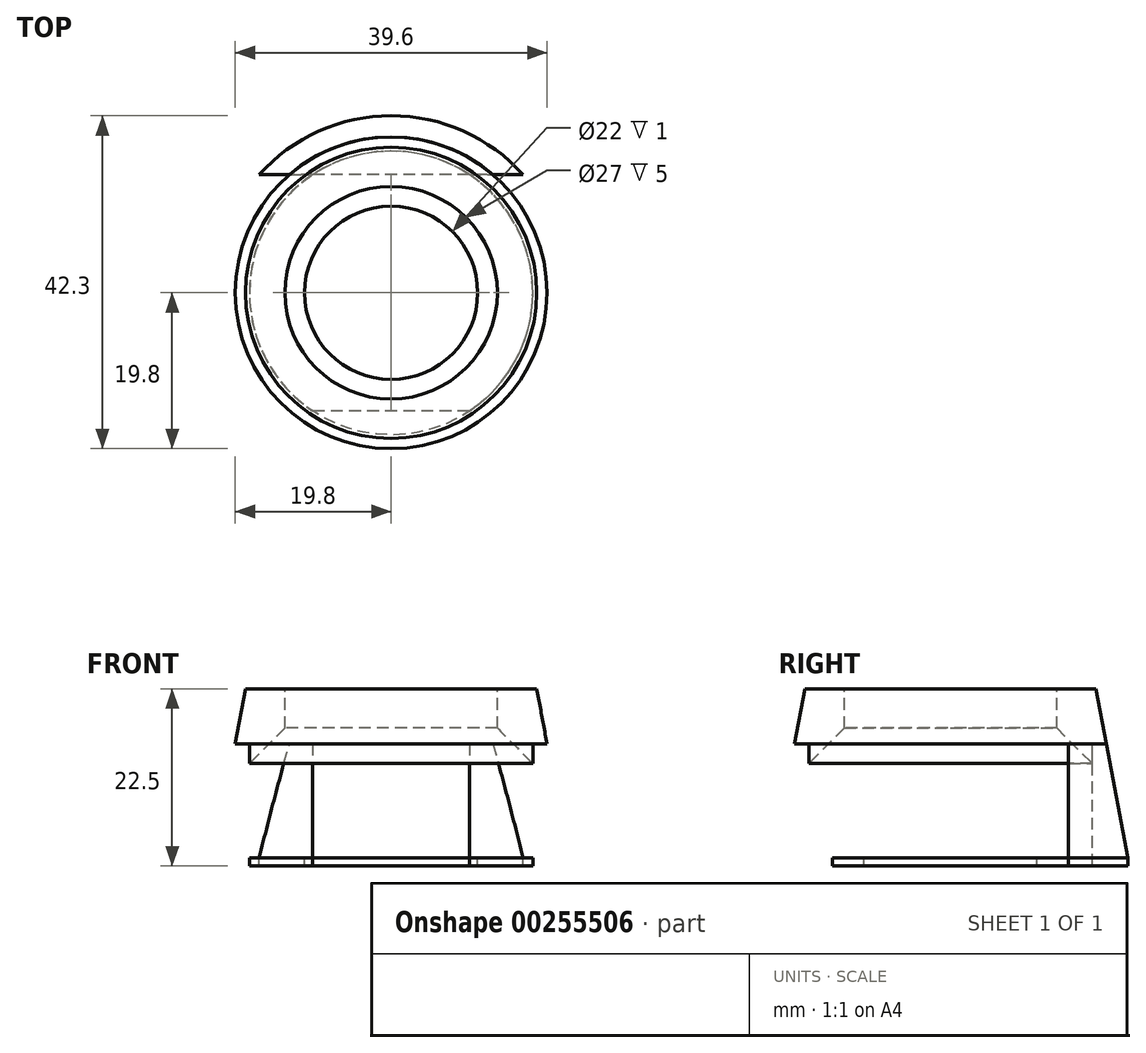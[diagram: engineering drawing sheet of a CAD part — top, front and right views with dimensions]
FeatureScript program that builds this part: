
annotation { "Feature Type Name" : "Feature", "Feature Type Description" : "" }
export const myFeature = defineFeature(function(context is Context, id is Id, definition is map)
    precondition{}
    {
        {
            var Q0;
            Q0=qCreatedBy(makeId("Top.planeOp"),FACE);
            var sketch = newSketch(context, id + "F0", { "sketchPlane" : qUnion([Q0])});
            skCircle(sketch, "E0", {"center": v(0, 0) * mm, "radius": 11 * mm});
            skCircle(sketch, "E1", {"center": v(0, 0) * mm, "radius": 18 * mm});
            skLineSegment(sketch, "E2.bottom", {"start": v(22.5, -15) * mm, "end": v(-22.5, -15) * mm});
            skLineSegment(sketch, "E2.top", {"start": v(22.5, 15) * mm, "end": v(-22.5, 15) * mm});
            skLineSegment(sketch, "E2.left", {"start": v(22.5, -15) * mm, "end": v(22.5, 15) * mm});
            skLineSegment(sketch, "E2.right", {"start": v(-22.5, -15) * mm, "end": v(-22.5, 15) * mm});
            skCircle(sketch, "E3", {"center": v(0, 0) * mm, "radius": 22.5 * mm});
            skSolve(sketch);
        }
        {
            var Q0;
            Q0=qCreatedBy(makeId("Front.planeOp"),FACE);
            var sketch = newSketch(context, id + "F1", { "sketchPlane" : qUnion([Q0])});
            skLineSegment(sketch, "E4.0.0", {"start": v(-9.95, 0) * mm, "end": v(-18, 0) * mm, "construction": true});
            skLineSegment(sketch, "E4.0.1", {"start": v(-9.95, 0) * mm, "end": v(-16.77, 0) * mm, "construction": true});
            skLineSegment(sketch, "E4.0.2", {"start": v(-16.77, 0) * mm, "end": v(-22.5, 0) * mm, "construction": true});
            skLineSegment(sketch, "E4.0.3", {"start": v(-22.5, 0) * mm, "end": v(-16.77, 0) * mm, "construction": true});
            skLineSegment(sketch, "E4.0.4", {"start": v(-16.77, 0) * mm, "end": v(-9.95, 0) * mm, "construction": true});
            skLineSegment(sketch, "E5", {"start": v(-18, 0) * mm, "end": v(-18, 12) * mm});
            skLineSegment(sketch, "E6", {"start": v(-18, 12) * mm, "end": v(-13.5, 16.5) * mm});
            skLineSegment(sketch, "E7", {"start": v(-13.5, 16.5) * mm, "end": v(-13.5, 21.5) * mm});
            skLineSegment(sketch, "E8", {"start": v(-13.5, 21.5) * mm, "end": v(-18.5, 21.5) * mm});
            skLineSegment(sketch, "E9", {"start": v(-18.5, 21.5) * mm, "end": v(-22.5, 0) * mm});
            skLineSegment(sketch, "E10", {"start": v(0, 35.02) * mm, "end": v(0, -30.21) * mm, "construction": true});
            skLineSegment(sketch, "E11", {"start": v(-18, 0) * mm, "end": v(-22.5, 0) * mm});
            skLineSegment(sketch, "E12", {"start": v(-18, 12) * mm, "end": v(-18, 14.5) * mm});
            skLineSegment(sketch, "E13", {"start": v(-18, 14.5) * mm, "end": v(-19.8, 14.5) * mm});
            skSolve(sketch);
        }
        {
            var Q0;
            Q0=makeQuery(id+"F1.imprint","IMPRINT",FACE,{"disambiguationData":[TD([[makeQuery(id+"F1.imprint","IMPRINT",EDGE,{"derivedFrom":sQuery(id+"F1.wireOp",EDGE,"E5")}),1.0]])]});
            var Q1;
            Q1=sQuery(id+"F1.wireOp",EDGE,"E10");
            revolve(context, id + "F2", {"entities" : qUnion([Q0]), "axis" : qUnion([Q1]), "revolveType" : RevolveType.FULL});
        }
        {
            var Q0;
            {var subQ0=sQuery(id+"F0.wireOp",EDGE,"E2.left");var subQ1=sQuery(id+"F0.wireOp",EDGE,"E2.bottom");var subQ2=makeQuery(id+"F0.imprint","INTERSECT",VERTEX,{"derivedFrom":[subQ1,subQ0]});Q0=makeQuery(id+"F0.imprint","IMPRINT",FACE,{"disambiguationData":[TD([[makeQuery(id+"F0.imprint","IMPRINT",EDGE,{"disambiguationData":[TD([[subQ2,-1.0]])],"derivedFrom":subQ1}),-1.0]])]});}
            var Q1;
            {var subQ1=sQuery(id+"F0.wireOp",EDGE,"E2.top");var subQ3=sQuery(id+"F0.wireOp",EDGE,"E1");var subQ4=makeQuery(id+"F0.imprint","INTERSECT",VERTEX,{"disambiguationData":[OD(1.0)],"derivedFrom":[subQ3,subQ1]});Q1=makeQuery(id+"F0.imprint","IMPRINT",FACE,{"disambiguationData":[TD([[makeQuery(id+"F0.imprint","IMPRINT",EDGE,{"disambiguationData":[TD([[subQ4,1.0]])],"derivedFrom":subQ3}),-1.0]])]});}
            var Q2;
            {var subQ0=sQuery(id+"F0.wireOp",EDGE,"E2.left");var subQ1=sQuery(id+"F0.wireOp",EDGE,"E2.top");var subQ2=makeQuery(id+"F0.imprint","INTERSECT",VERTEX,{"derivedFrom":[subQ1,subQ0]});Q2=makeQuery(id+"F0.imprint","IMPRINT",FACE,{"disambiguationData":[TD([[makeQuery(id+"F0.imprint","IMPRINT",EDGE,{"disambiguationData":[TD([[subQ2,-1.0]])],"derivedFrom":subQ1}),1.0]])]});}
            var Q3;
            Q3=makeQuery(id+"F0.imprint","IMPRINT",FACE,{"disambiguationData":[TD([[makeQuery(id+"F0.imprint","IMPRINT",EDGE,{"derivedFrom":sQuery(id+"F0.wireOp",EDGE,"E0")}),-1.0]])]});
            var Q4;
            Q4=makeQuery(id+"F0.imprint","IMPRINT",FACE,{"disambiguationData":[TD([[makeQuery(id+"F0.imprint","IMPRINT",EDGE,{"derivedFrom":sQuery(id+"F0.wireOp",EDGE,"E0")}),1.0]])]});
            var Q5;
            {var subQ1=sQuery(id+"F0.wireOp",EDGE,"E2.top");var subQ6=sQuery(id+"F0.wireOp",EDGE,"E1");var subQ8=makeQuery(id+"F0.imprint","INTERSECT",VERTEX,{"disambiguationData":[OD(0.0)],"derivedFrom":[subQ6,subQ1]});Q5=makeQuery(id+"F0.imprint","IMPRINT",FACE,{"disambiguationData":[TD([[makeQuery(id+"F0.imprint","IMPRINT",EDGE,{"disambiguationData":[TD([[subQ8,-1.0]])],"derivedFrom":subQ6}),-1.0]])]});}
            extrude(context, id + "F3", {"entities" : qUnion([Q0, Q1, Q2, Q3, Q4, Q5]), "operationType" : NewBodyOperationType.INTERSECT, "depth" : 25 * mm});
        }
        {
            var Q0;
            {var subQ1=sQuery(id+"F0.wireOp",EDGE,"E2.top");var subQ3=sQuery(id+"F0.wireOp",EDGE,"E1");var subQ4=makeQuery(id+"F0.imprint","INTERSECT",VERTEX,{"disambiguationData":[OD(1.0)],"derivedFrom":[subQ3,subQ1]});Q0=makeQuery(id+"F0.imprint","IMPRINT",FACE,{"disambiguationData":[TD([[makeQuery(id+"F0.imprint","IMPRINT",EDGE,{"disambiguationData":[TD([[subQ4,1.0]])],"derivedFrom":subQ3}),-1.0]])]});}
            var Q1;
            Q1=makeQuery(id+"F0.imprint","IMPRINT",FACE,{"disambiguationData":[TD([[makeQuery(id+"F0.imprint","IMPRINT",EDGE,{"derivedFrom":sQuery(id+"F0.wireOp",EDGE,"E0")}),-1.0]])]});
            var Q2;
            {var subQ1=sQuery(id+"F0.wireOp",EDGE,"E2.top");var subQ6=sQuery(id+"F0.wireOp",EDGE,"E1");var subQ8=makeQuery(id+"F0.imprint","INTERSECT",VERTEX,{"disambiguationData":[OD(0.0)],"derivedFrom":[subQ6,subQ1]});Q2=makeQuery(id+"F0.imprint","IMPRINT",FACE,{"disambiguationData":[TD([[makeQuery(id+"F0.imprint","IMPRINT",EDGE,{"disambiguationData":[TD([[subQ8,-1.0]])],"derivedFrom":subQ6}),-1.0]])]});}
            extrude(context, id + "F4", {"entities" : qUnion([Q0, Q1, Q2]), "operationType" : NewBodyOperationType.ADD, "oppositeDirection" : true, "depth" : 1 * mm});
        }
        {
            var Q0;
            Q0=makeQuery(id+"F1.imprint","IMPRINT",FACE,{"disambiguationData":[TD([[makeQuery(id+"F1.imprint","IMPRINT",EDGE,{"derivedFrom":sQuery(id+"F1.wireOp",EDGE,"E6")}),1.0]])]});
            var Q1;
            Q1=sQuery(id+"F1.wireOp",EDGE,"E10");
            revolve(context, id + "F5", {"entities" : qUnion([Q0]), "axis" : qUnion([Q1]), "revolveType" : RevolveType.FULL});
        }
    });
